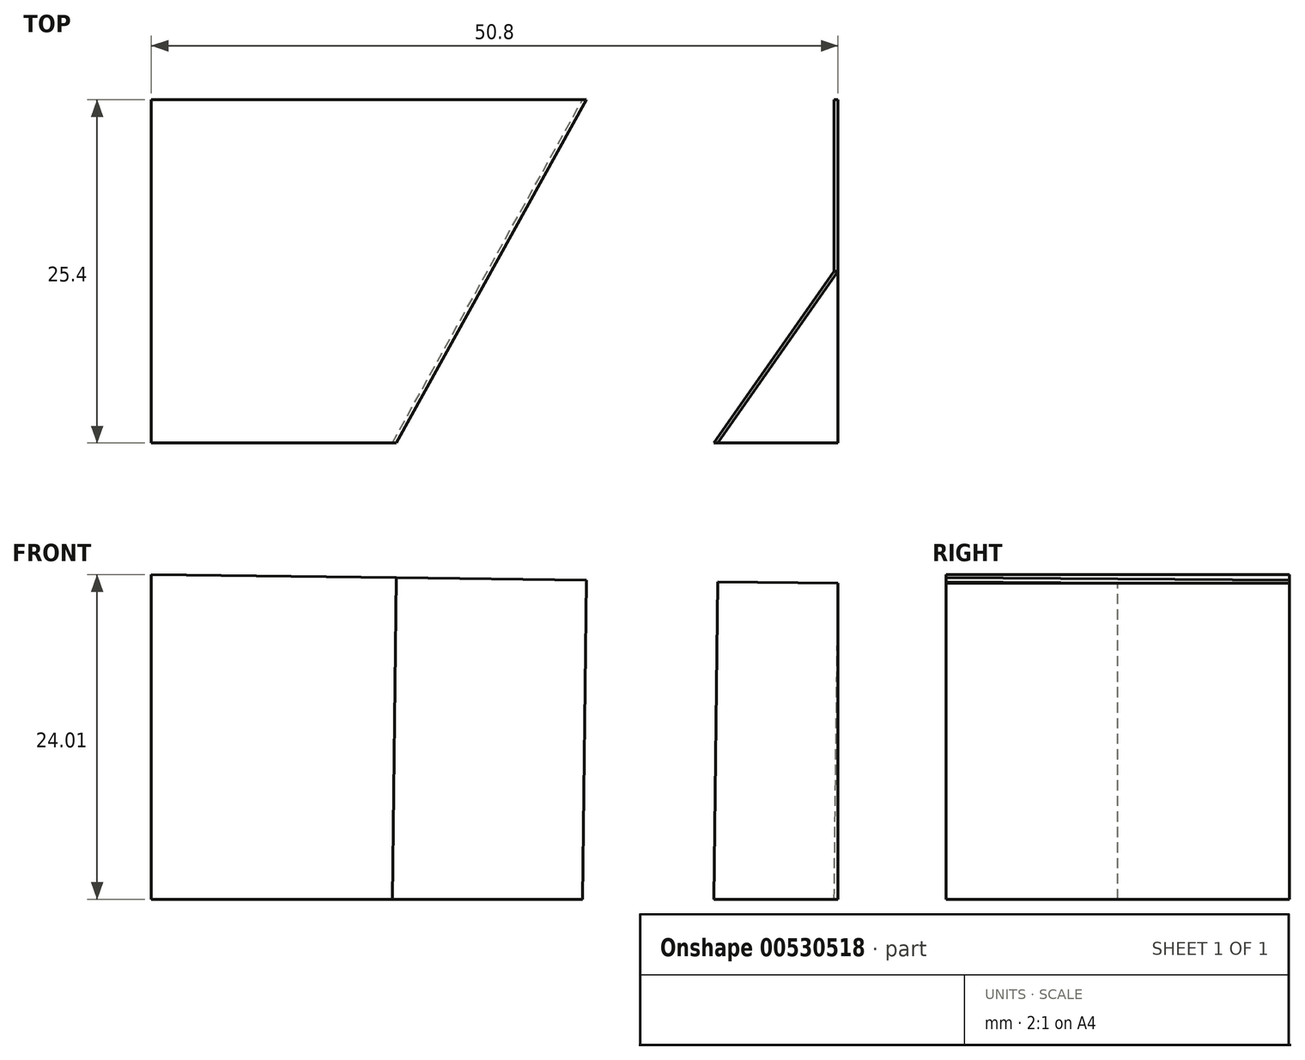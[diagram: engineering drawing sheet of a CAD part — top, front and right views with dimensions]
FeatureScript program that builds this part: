
annotation { "Feature Type Name" : "Feature", "Feature Type Description" : "" }
export const myFeature = defineFeature(function(context is Context, id is Id, definition is map)
    precondition{}
    {
        {
            var Q0;
            Q0=qCreatedBy(makeId("Front.planeOp"),FACE);
            var sketch = newSketch(context, id + "F0", { "sketchPlane" : qUnion([Q0])});
            skLineSegment(sketch, "E0", {"start": v(-36.75, 17.03) * mm, "end": v(-36.75, -6.98) * mm});
            skLineSegment(sketch, "E1", {"start": v(-36.75, -6.98) * mm, "end": v(14.05, -6.98) * mm});
            skLineSegment(sketch, "E2", {"start": v(14.05, -9) * mm, "end": v(14.05, 16.4) * mm});
            skLineSegment(sketch, "E3", {"start": v(14.05, 16.4) * mm, "end": v(-36.75, 17.03) * mm});
            skSolve(sketch);
        }
        {
            var Q0;
            Q0=makeQuery(id+"F0.imprint","IMPRINT",FACE,{"disambiguationData":[TD([[makeQuery(id+"F0.imprint","IMPRINT",EDGE,{"derivedFrom":sQuery(id+"F0.wireOp",EDGE,"E0")}),1.0]])]});
            extrude(context, id + "F1", {"entities" : qUnion([Q0]), "depth" : 25.4 * mm, "offsetDistance" : 25.4 * mm});
        }
        {
            var Q0;
            Q0=makeQuery(id+"F1.opExtrude","SWEPT_FACE",FACE,{"disambiguationData":[OSD([sQuery(id+"F0.wireOp",EDGE,"E3")])]});
            var sketch = newSketch(context, id + "F2", { "sketchPlane" : qUnion([Q0])});
            skLineSegment(sketch, "E4", {"start": v(-18.84, -25.4) * mm, "end": v(-4.76, 0) * mm});
            skLineSegment(sketch, "E5", {"start": v(4.96, -25.4) * mm, "end": v(13.85, -12.7) * mm});
            skLineSegment(sketch, "E6", {"start": v(13.85, -12.7) * mm, "end": v(13.85, 0) * mm});
            skLineSegment(sketch, "E7", {"start": v(13.85, 0) * mm, "end": v(-4.76, 0) * mm});
            skLineSegment(sketch, "E8", {"start": v(-18.84, -25.4) * mm, "end": v(4.96, -25.4) * mm});
            skSolve(sketch);
        }
        {
            var Q0;
            Q0 = qSketchRegion(id + "F2", true);
            extrude(context, id + "F3", {"entities" : qUnion([Q0]), "operationType" : NewBodyOperationType.REMOVE, "oppositeDirection" : true, "depth" : 25.4 * mm, "offsetDistance" : 25.4 * mm});
        }
    });
